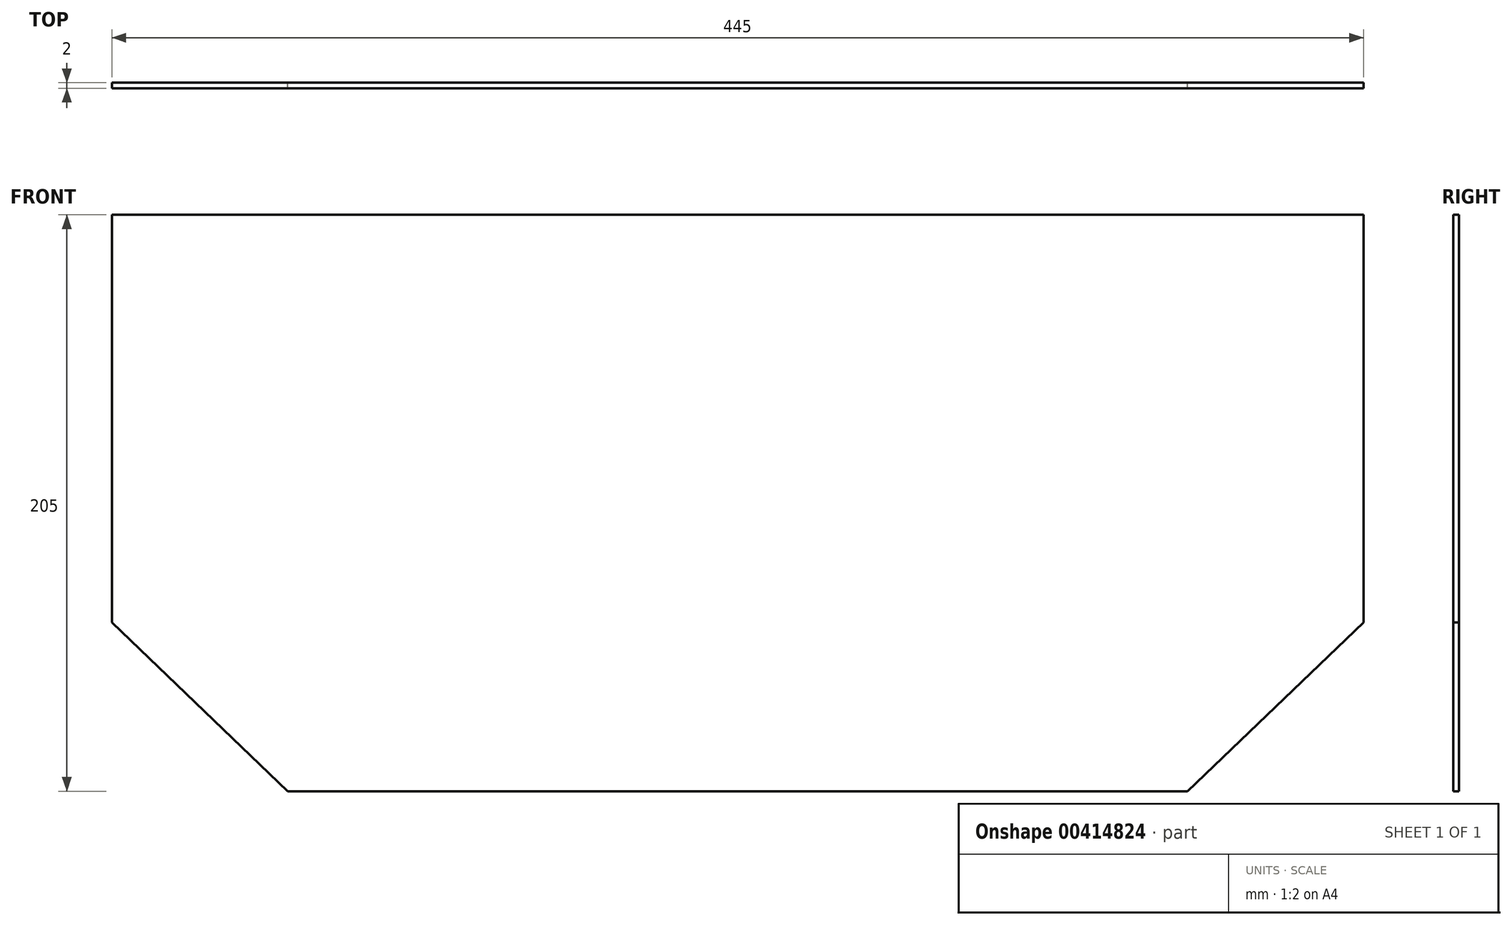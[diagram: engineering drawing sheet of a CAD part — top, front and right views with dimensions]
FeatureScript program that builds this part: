
annotation { "Feature Type Name" : "Feature", "Feature Type Description" : "" }
export const myFeature = defineFeature(function(context is Context, id is Id, definition is map)
    precondition{}
    {
        {
            var Q0;
            Q0=qCreatedBy(makeId("Front.planeOp"),FACE);
            var sketch = newSketch(context, id + "F0", { "sketchPlane" : qUnion([Q0])});
            skLineSegment(sketch, "E0", {"start": v(0, 0) * mm, "end": v(0, 302.05) * mm, "construction": true});
            skLineSegment(sketch, "E1", {"start": v(0, 205) * mm, "end": v(-222.5, 205) * mm});
            skLineSegment(sketch, "E2", {"start": v(-222.5, 205) * mm, "end": v(-222.5, 60) * mm});
            skLineSegment(sketch, "E3", {"start": v(-222.5, 60) * mm, "end": v(-160, 0) * mm});
            skLineSegment(sketch, "E4", {"start": v(-160, 0) * mm, "end": v(0, 0) * mm});
            skLineSegment(sketch, "E5.MirrorCS", {"start": v(222.5, 205) * mm, "end": v(222.5, 60) * mm});
            skLineSegment(sketch, "E6.MirrorCS", {"start": v(222.5, 60) * mm, "end": v(160, 0) * mm});
            skLineSegment(sketch, "E7.MirrorCS", {"start": v(0, 205) * mm, "end": v(222.5, 205) * mm});
            skLineSegment(sketch, "E8.MirrorCS", {"start": v(160, 0) * mm, "end": v(0, 0) * mm});
            skSolve(sketch);
        }
        {
            var Q0;
            Q0 = qSketchRegion(id + "F0", true);
            extrude(context, id + "F1", {"entities" : qUnion([Q0]), "depth" : 2 * mm});
        }
    });
